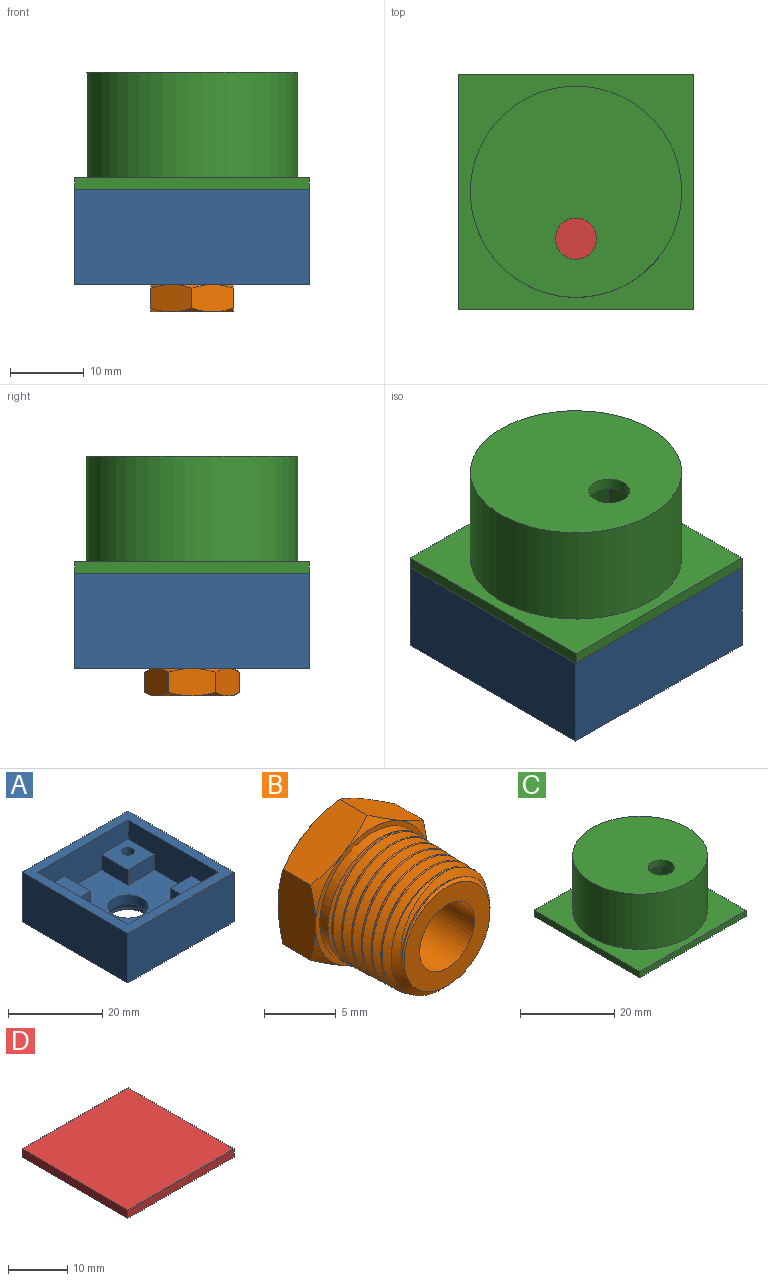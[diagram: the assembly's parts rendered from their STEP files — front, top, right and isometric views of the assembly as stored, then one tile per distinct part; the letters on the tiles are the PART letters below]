
ASSEMBLY  parts=4 mates=6
PART A: 30 faces, bbox 31.8x31.8x12.9 mm
  f0: cylinder r=4.5mm len=9mm, axis (0,0,-1), area 17.5mm2, adj f12,f29
  f1: plane 26.99x26.99mm, normal (0,0,1), area 475mm2, adj f2,f3,f4,f9,f11,f13,f14,f16
  f2: plane 26.99x8.89mm, normal (0,1,0), area 189.5mm2, adj f1,f3,f9,f10,f20,f21,f23,f24
  f3: plane 26.99x8.89mm, normal (-1,0,0), area 176.9mm2, adj f1,f2,f4,f10,f17,f18,f19,f21
  f4: plane 26.99x8.89mm, normal (0,-1,0), area 176.9mm2, adj f1,f3,f9,f10,f14,f15,f16,f18
  f5: plane 31.75x12.86mm, normal (1,0,0), area 408.3mm2, adj f6,f8,f10,f29
  f6: plane 31.75x12.86mm, normal (0,1,0), area 408.3mm2, adj f5,f7,f10,f29
  f7: plane 31.75x12.86mm, normal (-1,0,0), area 408.3mm2, adj f6,f8,f10,f29
  f8: plane 31.75x12.86mm, normal (0,-1,0), area 408.3mm2, adj f5,f7,f10,f29
  f9: plane 26.99x8.89mm, normal (1,0,0), area 195.8mm2, adj f1,f2,f4,f10,f13,f15,f22,f24
  f10: plane 31.75x31.75mm, normal (0,0,1), area 279.7mm2, adj f2,f3,f4,f5,f6,f7,f8,f9
  f11: cylinder r=4.25mm len=8.5mm, axis (0,0,-1), area 62.8mm2, adj f1,f12
  f12: cone r=4.25mm half-angle=14deg, axis (0,0,-1), area 28.3mm2, adj f0,f11
  f13: plane 7.94x3.97mm, normal (0,-1,0), area 31.5mm2, adj f1,f9,f14,f15
  f14: plane 7.94x3.97mm, normal (1,0,0), area 31.5mm2, adj f1,f4,f13,f15
  f15: plane 7.94x7.94mm, normal (0,0,1), area 56.9mm2, adj f4,f9,f13,f14,f28
  f16: plane 7.94x3.97mm, normal (-1,0,0), area 31.5mm2, adj f1,f4,f17,f18
  f17: plane 7.94x3.97mm, normal (0,-1,0), area 31.5mm2, adj f1,f3,f16,f18
  f18: plane 7.94x7.94mm, normal (0,0,1), area 56.9mm2, adj f3,f4,f16,f17,f26
  f19: plane 6.35x3.97mm, normal (0,1,0), area 25.2mm2, adj f1,f3,f20,f21
  f20: plane 7.94x3.97mm, normal (-1,0,0), area 31.5mm2, adj f1,f2,f19,f21
  f21: plane 7.94x6.35mm, normal (0,0,1), area 50.4mm2, adj f2,f3,f19,f20
  f22: plane 6.35x3.97mm, normal (0,1,0), area 25.2mm2, adj f1,f9,f23,f24
  f23: plane 3.97x3.18mm, normal (1,0,0), area 12.6mm2, adj f1,f2,f22,f24
  f24: plane 6.35x3.18mm, normal (0,0,1), area 20.2mm2, adj f2,f9,f22,f23
  f25: cone r=0mm half-angle=59deg, axis (0,0,1), area 7.2mm2, adj f26
  f26: cylinder r=1.4mm len=6.35mm, axis (0,0,1), area 55.7mm2, adj f18,f25
  f27: cone r=0mm half-angle=59deg, axis (0,0,1), area 7.2mm2, adj f28
  f28: cylinder r=1.4mm len=6.35mm, axis (0,0,1), area 55.7mm2, adj f15,f27
  f29: plane 31.75x31.75mm, normal (0,0,-1), area 944.4mm2, adj f0,f5,f6,f7,f8
PART B: 37 faces, bbox 13.4x11.9x13.4 mm
  f0: cone r=4.77mm half-angle=45deg, axis (0,1,0), area 5.5mm2, adj f3,f33
  f1: cone r=4.6mm half-angle=45deg, axis (0,-1,0), area 5.3mm2, adj f2,f36
  f2: cylinder r=4.72mm len=9.45mm, axis (0,1,0), area 32.9mm2, adj f1,f35
  f3: cylinder r=4.77mm len=9.55mm, axis (0,1,0), area 33.2mm2, adj f0,f35
  f4: cylinder r=2.71mm len=7.41mm, axis (0,-1,0), area 126.1mm2, adj f12,f34
  f5: cone r=5.56mm half-angle=60deg, axis (0,-1,0), area 3mm2, adj f19,f20,f33
  f6: cone r=5.56mm half-angle=60deg, axis (0,1,0), area 3mm2, adj f16,f17,f22
  f7: cone r=5.14mm half-angle=70deg, axis (0,1,0), area 9.8mm2, adj f8,f13,f14,f15
  f8: cylinder r=5.14mm len=10.29mm, axis (0,-1,0), area 26mm2, adj f7,f11,f16
  f9: cone r=4.96mm half-angle=45deg, axis (0,1,0), area 16.9mm2, adj f10,f11,f12,f13,f14,f15
  f10: cone r=4.96mm half-angle=45deg, axis (0,1,0), area 0mm2, adj f9,f11,f15
  f11: cone r=5.14mm half-angle=1.8deg, axis (0,1,0), area 31.5mm2, adj f8,f9,f10,f13,f15
  f12: plane 8.47x8.47mm, normal (0,-1,0), area 33.2mm2, adj f4,f9
  f13: bspline ~10.33x10.3mm, area -2.2mm2, adj f7,f9,f11,f14
  f14: bspline ~9.14x9.11mm, area 21.9mm2, adj f7,f9,f13,f15
  f15: bspline ~10.23x10.17mm, area 135.9mm2, adj f7,f9,f10,f11,f14
  f16: plane 11.11x11.11mm, normal (0,-1,0), area 13.9mm2, adj f6,f8,f23,f24,f25,f26,f27
  f17: plane 6.08x4.23mm, normal (0.5,0,-0.87), area 21.6mm2, adj f6,f18,f22,f26,f30,f31
  f18: plane 6.95x4.23mm, normal (1,0,0), area 21.6mm2, adj f17,f19,f26,f27,f31,f32
  f19: plane 6.08x4.23mm, normal (0.5,0,0.87), area 21.6mm2, adj f5,f18,f20,f23,f27,f32
  f20: plane 6.08x4.23mm, normal (-0.5,0,0.87), area 21.6mm2, adj f5,f19,f21,f23,f24,f28
  f21: plane 6.95x4.23mm, normal (-1,0,0), area 21.6mm2, adj f20,f22,f24,f25,f28,f29
  f22: plane 6.08x4.23mm, normal (-0.5,0,-0.87), area 21.6mm2, adj f6,f17,f21,f25,f29,f30
  f23: cone r=5.56mm half-angle=60deg, axis (0,1,0), area 3mm2, adj f16,f19,f20
  f24: cone r=5.56mm half-angle=60deg, axis (0,1,0), area 3mm2, adj f16,f20,f21
  f25: cone r=5.56mm half-angle=60deg, axis (0,1,0), area 3mm2, adj f16,f21,f22
  f26: cone r=5.56mm half-angle=60deg, axis (0,1,0), area 3mm2, adj f16,f17,f18
  f27: cone r=5.56mm half-angle=60deg, axis (0,1,0), area 3mm2, adj f16,f18,f19
  f28: cone r=5.56mm half-angle=60deg, axis (0,-1,0), area 3mm2, adj f20,f21,f33
  f29: cone r=5.56mm half-angle=60deg, axis (0,-1,0), area 3mm2, adj f21,f22,f33
  f30: cone r=5.56mm half-angle=60deg, axis (0,-1,0), area 3mm2, adj f17,f22,f33
  f31: cone r=5.56mm half-angle=60deg, axis (0,-1,0), area 3mm2, adj f17,f18,f33
  f32: cone r=5.56mm half-angle=60deg, axis (0,-1,0), area 3mm2, adj f18,f19,f33
  f33: plane 11.11x11.11mm, normal (0,1,0), area 21.5mm2, adj f0,f5,f28,f29,f30,f31,f32
  f34: plane 5.42x5.42mm, normal (0,-1,0), area 23.1mm2, adj f4
  f35: plane 9.55x9.55mm, normal (0,1,0), area 1.5mm2, adj f2,f3
  f36: plane 9.19x9.19mm, normal (0,1,0), area 66.4mm2, adj f1
PART C: 23 faces, bbox 31.8x31.8x17.5 mm
  f0: cylinder r=12.7mm len=15.88mm, axis (0,0,1), area 140.7mm2, adj f6,f10,f12,f22
  f1: cylinder r=12.7mm len=15.88mm, axis (0,0,1), area 140.7mm2, adj f7,f8,f12,f22
  f2: cylinder r=12.7mm len=15.88mm, axis (0,0,1), area 140.7mm2, adj f8,f10,f12,f22
  f3: plane 26.19x1.59mm, normal (1,0,0), area 41.6mm2, adj f4,f11,f12,f13
  f4: plane 26.19x1.59mm, normal (0,1,0), area 41.6mm2, adj f3,f5,f12,f13
  f5: plane 26.19x1.59mm, normal (-1,0,0), area 41.6mm2, adj f4,f11,f12,f13
  f6: plane 15.88x10.74mm, normal (1,0,0), area 170.5mm2, adj f0,f9,f12,f22
  f7: plane 15.88x10.74mm, normal (0,-1,0), area 170.5mm2, adj f1,f9,f12,f22
  f8: plane 15.88x10.74mm, normal (-1,0,0), area 170.5mm2, adj f1,f2,f12,f22
  f9: cylinder r=12.7mm len=15.88mm, axis (0,0,1), area 140.7mm2, adj f6,f7,f12,f22
  f10: plane 15.88x10.74mm, normal (0,1,0), area 170.5mm2, adj f0,f2,f12,f22
  f11: plane 26.19x1.59mm, normal (0,-1,0), area 41.6mm2, adj f3,f5,f12,f13
  f12: plane 26.19x26.19mm, normal (0,0,-1), area 213.8mm2, adj f0,f1,f2,f3,f4,f5,f6,f7
  f13: plane 31.75x31.75mm, normal (0,0,-1), area 321.9mm2, adj f3,f4,f5,f11,f15,f16,f17,f18
  f14: plane 31.75x31.75mm, normal (0,0,1), area 366.8mm2, adj f15,f16,f17,f18,f19
  f15: plane 31.75x1.59mm, normal (0,-1,0), area 50.4mm2, adj f13,f14,f16,f18
  f16: plane 31.75x1.59mm, normal (-1,0,0), area 50.4mm2, adj f13,f14,f15,f17
  f17: plane 31.75x1.59mm, normal (0,1,0), area 50.4mm2, adj f13,f14,f16,f18
  f18: plane 31.75x1.59mm, normal (1,0,0), area 50.4mm2, adj f13,f14,f15,f17
  f19: cylinder r=14.29mm len=28.58mm, axis (0,0,-1), area 1282.6mm2, adj f14,f21
  f20: cylinder r=2.78mm len=5.56mm, axis (0,0,-1), area 27.7mm2, adj f21,f22
  f21: plane 28.58x28.58mm, normal (0,0,1), area 617.1mm2, adj f19,f20
  f22: plane 23.02x23.02mm, normal (0,0,-1), area 448mm2, adj f0,f1,f2,f6,f7,f8,f9,f10
PART D: 6 faces, bbox 25.4x25.4x1.7 mm
  f0: plane 25.4x1.7mm, normal (1,0,0), area 43.2mm2, adj f1,f3,f4,f5
  f1: plane 25.4x1.7mm, normal (0,1,0), area 43.2mm2, adj f0,f2,f4,f5
  f2: plane 25.4x1.7mm, normal (-1,0,0), area 43.2mm2, adj f1,f3,f4,f5
  f3: plane 25.4x1.7mm, normal (0,-1,0), area 43.2mm2, adj f0,f2,f4,f5
  f4: plane 25.4x25.4mm, normal (0,0,1), area 645.2mm2, adj f0,f1,f2,f3
  f5: plane 25.4x25.4mm, normal (0,0,-1), area 645.2mm2, adj f0,f1,f2,f3
PLACE A t=(-56.2,32.63,30.24)mm
PLACE B rot(axis=(-1,0,0),90deg) t=(-56.2,32.63,28.12)mm
PLACE C t=(-56.2,32.63,30.24)mm fixed
PLACE D rot(axis=(1,0,0),180deg) t=(-56.2,32.63,36.14)mm
MATE planar A.f5 <-> C.f18  axis (1,0,0) through (-40.33,32.63,32.7)mm
MATE planar C.f0 <-> A.f0  axis (0,0,-1) through (-56.2,32.63,39.13)mm
MATE fastened D.f4 <-> B.f0  axis (0,0,-1) through (-56.2,32.63,34.44)mm
MATE planar B.f0 <-> A.f0  axis (0,0,1) through (-56.2,32.63,26.27)mm
MATE cylindrical B.f0 <-> A.f0  axis (0,0,1) through (-56.2,32.63,33.68)mm
MATE planar C.f17 <-> A.f6  axis (0,1,0) through (-56.2,48.51,39.92)mm
